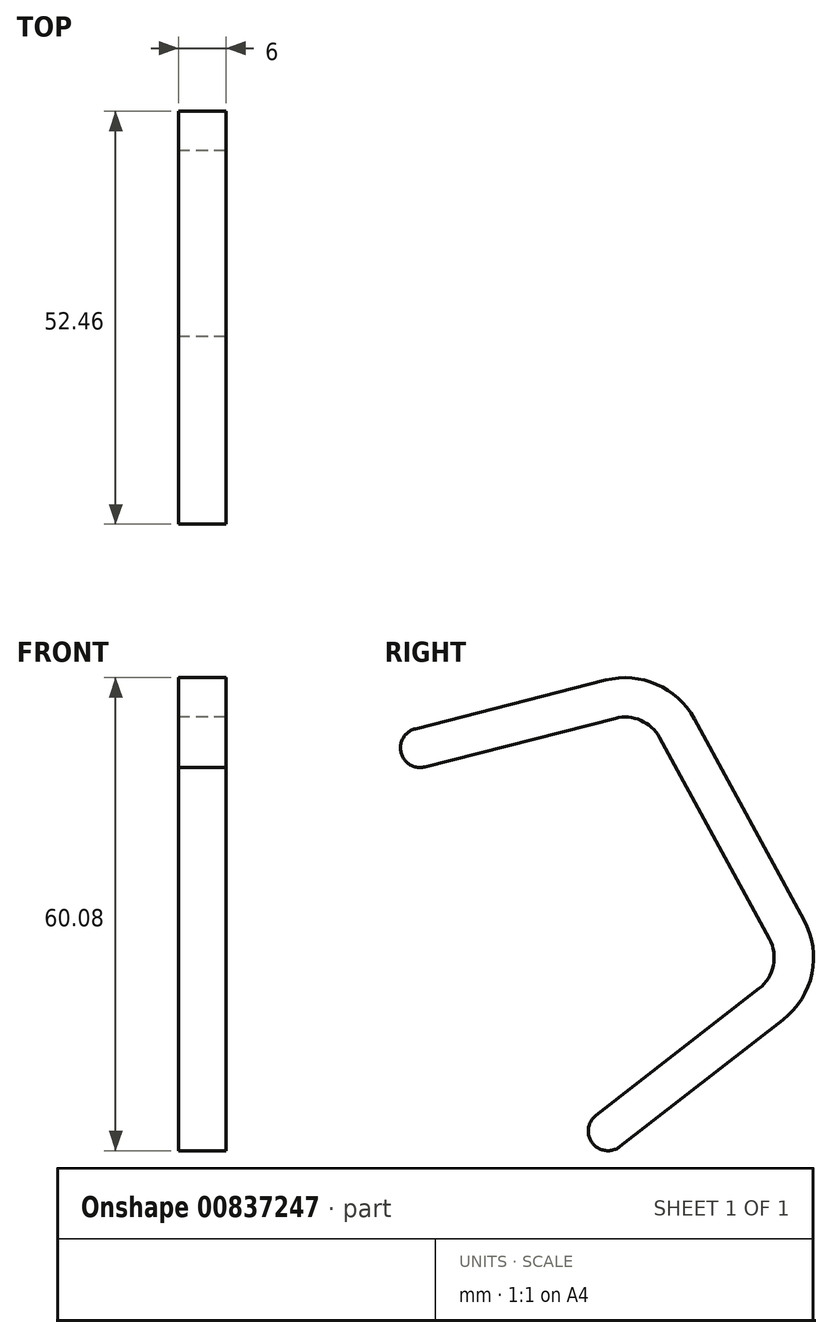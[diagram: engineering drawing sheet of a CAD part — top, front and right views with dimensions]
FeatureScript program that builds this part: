
annotation { "Feature Type Name" : "Feature", "Feature Type Description" : "" }
export const myFeature = defineFeature(function(context is Context, id is Id, definition is map)
    precondition{}
    {
        {
            var Q0;
            Q0=qCreatedBy(makeId("Right.planeOp"),FACE);
            var sketch = newSketch(context, id + "F0", { "sketchPlane" : qUnion([Q0])});
            skLineSegment(sketch, "E0", {"start": v(-15.05, 9.18) * mm, "end": v(9.13, 15.36) * mm});
            skLineSegment(sketch, "E1", {"start": v(14.75, 12.9) * mm, "end": v(28.69, -12.64) * mm});
            skLineSegment(sketch, "E2", {"start": v(27.37, -18.99) * mm, "end": v(6.65, -35.1) * mm});
            skLineSegment(sketch, "E3.0", {"start": v(-16.28, 14.03) * mm, "end": v(7.89, 20.2) * mm});
            skLineSegment(sketch, "E4.0", {"start": v(19.14, 15.3) * mm, "end": v(33.08, -10.25) * mm});
            skLineSegment(sketch, "E5.0", {"start": v(30.44, -22.93) * mm, "end": v(9.72, -39.05) * mm});
            skArc(sketch, "E6", {"start": v(-16.28, 14.03) * mm, "mid": v(-18.09, 10.99) * mm, "end": v(-15.05, 9.18) * mm});
            skArc(sketch, "E7", {"start": v(6.65, -35.1) * mm, "mid": v(6.21, -38.6) * mm, "end": v(9.72, -39.05) * mm});
            skPoint(sketch, "E8.visualSharp", {"position": v(12.9, 16.32) * mm});
            skArc(sketch, "E8.filletArc", {"start": v(14.75, 12.9) * mm, "mid": v(12.36, 15.1) * mm, "end": v(9.13, 15.36) * mm});
            skArc(sketch, "E9.filletArc", {"start": v(19.14, 15.3) * mm, "mid": v(14.36, 19.68) * mm, "end": v(7.89, 20.2) * mm});
            skPoint(sketch, "E10.visualSharp", {"position": v(30.72, -16.38) * mm});
            skArc(sketch, "E10.filletArc", {"start": v(27.37, -18.99) * mm, "mid": v(29.2, -16.06) * mm, "end": v(28.69, -12.64) * mm});
            skArc(sketch, "E11.filletArc", {"start": v(30.44, -22.93) * mm, "mid": v(34.1, -17.08) * mm, "end": v(33.08, -10.25) * mm});
            skSolve(sketch);
        }
        {
            var Q0;
            Q0 = qSketchRegion(id + "F0", true);
            extrude(context, id + "F1", {"entities" : qUnion([Q0]), "depth" : 6 * mm, "offsetDistance" : 25.4 * mm});
        }
    });
